# Revit family: Power-Teknion-BEEPC_Power_Cube-R2018
name_source: partatom
category: Furniture
revit_build: Autodesk Revit 2018 (Build: 20190510_1515(x64)
units: mm (PartAtom-declared; Revit-internal decimal feet)

## family parameters
Always vertical = Yes
Cut with Voids When Loaded = No
OmniClass Number = 23.40.20.00
OmniClass Title = General Furniture and Specialties
Room Calculation Point = No
Shared = Yes
Work Plane-Based = Yes

## types (7) — shared parameters
Assembly Code = E2020200
Default Elevation = 48 "
Manufacturer = Teknion
Manufacturer Fax = 416.661.4586
Part Number = BEEPC
Product Documentation Link = https://www.teknion.com
Product Line = Expansion Casegoods
Product Page URL = https://www.teknion.com
Series = Expansion Casegoods
Sustainability Data = https://www.teknion.com
URL = www.teknion.com
Unit Weight URL = http://www.teknion.com
Warranty = http://www.teknion.com

## per-type parameters (varying)
| type | Description | Dual | Dual - Data | Dual - Power | Dual - USB | Model | Quad | Quad - Left Data | Quad - Left USB | Quad - Power | Quad - Right Data | Quad - Right USB | Width |
| Dual - 1 Power / 0 USB / 1 Data | Power Cube, Dual - 1 Power / 0 USB / 1 Data Configuration | Yes | Yes | No | No | BEEPCD101 | No | No | No | No | No | No | 5 " |
| Quad - 2 Power / 0 USB / 2 Data | Power Cube, Quad - 2 Power / 0 USB / 2 Data Configuration | No | No | No | No | BEEPCQ202 | Yes | Yes | No | No | Yes | No | 7.559 " |
| Dual - 1 Power / 2 USB / 0 Data | Power Cube, Dual - 1 Power / 2 USB / 0 Data Configuration | Yes | No | No | Yes | BEEPCD120 | No | No | No | No | No | No | 5 " |
| Dual - Power Only | Power Cube, Dual - Power Only Configuration | Yes | No | Yes | No | BEEPCD200 | No | No | No | No | No | No | 5 " |
| Quad - 2 Power / 2 USB / 1 Data | Power Cube, Quad - 2 Power / 2 USB / 1 Data Configuration | No | No | No | No | BEEPCQ221 | Yes | Yes | No | No | No | Yes | 7.559 " |
| Quad - 2 Power / 4 USB / 0 Data | Power Cube, Quad - 2 Power / 4 USB / 0 Data Configuration | No | No | No | No | BEEPCQ240 | Yes | No | Yes | No | No | Yes | 7.559 " |
| Quad - 3 Power / 2 USB / 0 Data | Power Cube, Quad - 3 Power / 2 USB / 0 Data Configuration | No | No | No | No | BEEPCQ320 | Yes | No | No | Yes | No | Yes | 7.559 " |

## geometry (parser evidence)
native form markers: Sweep x2
no freeform markers — native parametric forms only
